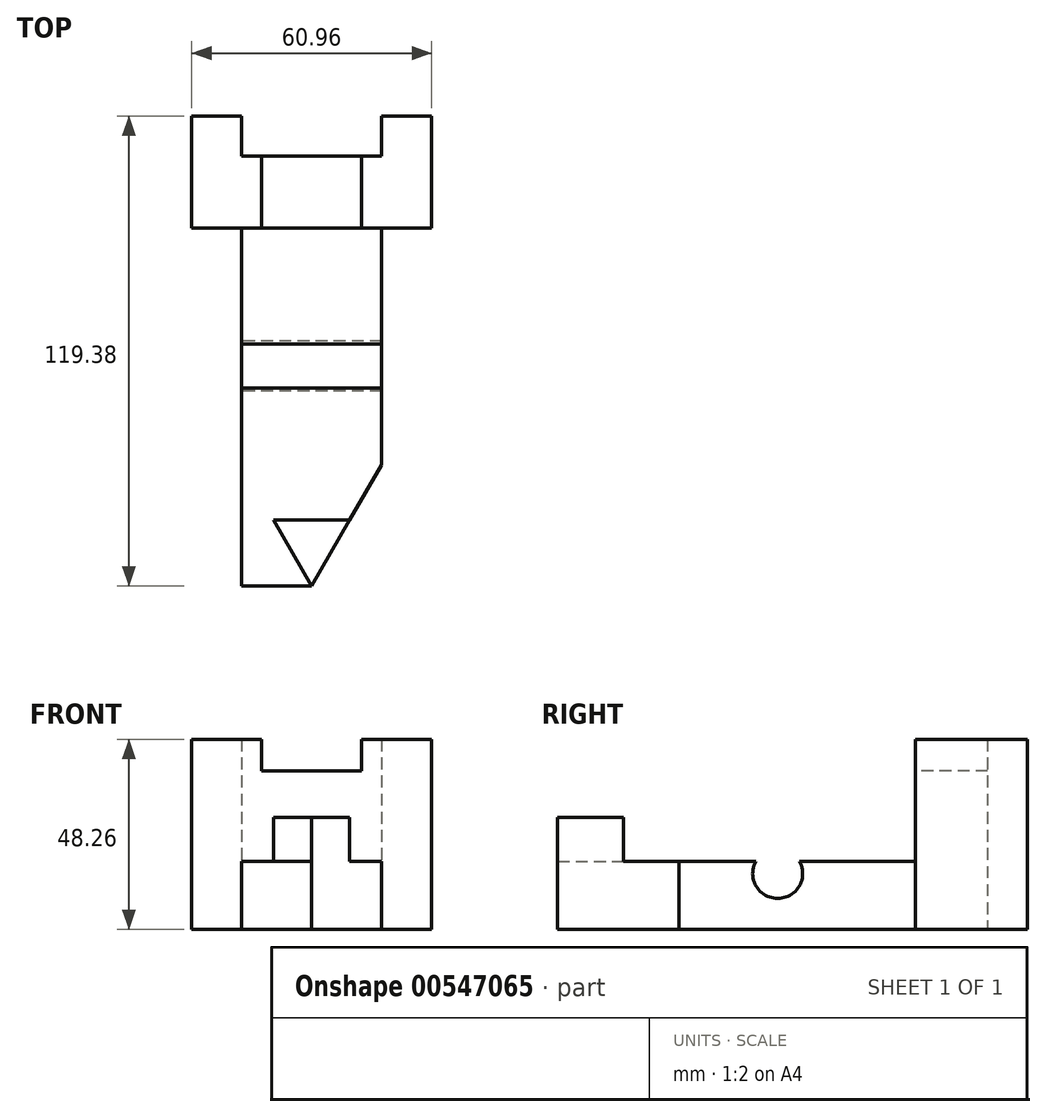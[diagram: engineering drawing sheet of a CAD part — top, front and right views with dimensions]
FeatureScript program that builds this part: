
annotation { "Feature Type Name" : "Feature", "Feature Type Description" : "" }
export const myFeature = defineFeature(function(context is Context, id is Id, definition is map)
    precondition{}
    {
        {
            var Q0;
            Q0=qCreatedBy(makeId("Front.planeOp"),FACE);
            var sketch = newSketch(context, id + "F0", { "sketchPlane" : qUnion([Q0])});
            skLineSegment(sketch, "E0.bottom", {"start": v(-43.38, 10.74) * mm, "end": v(17.58, 10.74) * mm});
            skLineSegment(sketch, "E0.top", {"start": v(-43.38, -37.52) * mm, "end": v(17.58, -37.52) * mm});
            skLineSegment(sketch, "E0.left", {"start": v(-43.38, 10.74) * mm, "end": v(-43.38, -37.52) * mm});
            skLineSegment(sketch, "E0.right", {"start": v(17.58, 10.74) * mm, "end": v(17.58, -37.52) * mm});
            skSolve(sketch);
        }
        {
            var Q0;
            Q0=makeQuery(id+"F0.imprint","IMPRINT",FACE,{"disambiguationData":[TD([[makeQuery(id+"F0.imprint","IMPRINT",EDGE,{"derivedFrom":sQuery(id+"F0.wireOp",EDGE,"E0.bottom")}),-1.0]])]});
            extrude(context, id + "F1", {"entities" : qUnion([Q0]), "depth" : 28.45 * mm, "offsetDistance" : 25.4 * mm});
        }
        {
            var Q0;
            Q0=makeQuery(id+"F1.opExtrude","CAP_FACE",FACE,{"disambiguationData":[OSD([sQuery(id+"F0.wireOp",EDGE,"E0.bottom"),sQuery(id+"F0.wireOp",EDGE,"E0.top"),sQuery(id+"F0.wireOp",EDGE,"E0.left"),sQuery(id+"F0.wireOp",EDGE,"E0.right")])],"isStart":false});
            var sketch = newSketch(context, id + "F2", { "sketchPlane" : qUnion([Q0])});
            skLineSegment(sketch, "E1.bottom", {"start": v(-25.6, 10.74) * mm, "end": v(-0.2, 10.74) * mm});
            skLineSegment(sketch, "E1.top", {"start": v(-25.6, 2.76) * mm, "end": v(-0.2, 2.76) * mm});
            skLineSegment(sketch, "E1.left", {"start": v(-25.6, 10.74) * mm, "end": v(-25.6, 2.76) * mm});
            skLineSegment(sketch, "E1.right", {"start": v(-0.2, 10.74) * mm, "end": v(-0.2, 2.76) * mm});
            skSolve(sketch);
        }
        {
            var Q0;
            Q0=makeQuery(id+"F2.imprint","IMPRINT",FACE,{"disambiguationData":[TD([[makeQuery(id+"F2.imprint","IMPRINT",EDGE,{"derivedFrom":sQuery(id+"F2.wireOp",EDGE,"E1.bottom")}),-1.0]])]});
            extrude(context, id + "F3", {"entities" : qUnion([Q0]), "operationType" : NewBodyOperationType.REMOVE, "oppositeDirection" : true, "depth" : 30.23 * mm, "offsetDistance" : 25.4 * mm});
        }
        {
            var Q0;
            Q0=makeQuery(id+"F1.opExtrude","CAP_FACE",FACE,{"disambiguationData":[OSD([sQuery(id+"F0.wireOp",EDGE,"E0.bottom"),sQuery(id+"F0.wireOp",EDGE,"E0.top"),sQuery(id+"F0.wireOp",EDGE,"E0.left"),sQuery(id+"F0.wireOp",EDGE,"E0.right")])],"isStart":true});
            var sketch = newSketch(context, id + "F4", { "sketchPlane" : qUnion([Q0])});
            skLineSegment(sketch, "E2.bottom", {"start": v(-4.88, 10.74) * mm, "end": v(30.68, 10.74) * mm});
            skLineSegment(sketch, "E2.top", {"start": v(-4.88, -37.52) * mm, "end": v(30.68, -37.52) * mm});
            skLineSegment(sketch, "E2.left", {"start": v(-4.88, 10.74) * mm, "end": v(-4.88, -37.52) * mm});
            skLineSegment(sketch, "E2.right", {"start": v(30.68, 10.74) * mm, "end": v(30.68, -37.52) * mm});
            skSolve(sketch);
        }
        {
            var Q0;
            Q0 = qSketchRegion(id + "F4", true);
            extrude(context, id + "F5", {"entities" : qUnion([Q0]), "operationType" : NewBodyOperationType.REMOVE, "oppositeDirection" : true, "depth" : 10.16 * mm, "offsetDistance" : 25.4 * mm});
        }
        {
            var Q0;
            Q0=makeQuery(id+"F1.opExtrude","CAP_FACE",FACE,{"disambiguationData":[OSD([sQuery(id+"F0.wireOp",EDGE,"E0.bottom"),sQuery(id+"F0.wireOp",EDGE,"E0.top"),sQuery(id+"F0.wireOp",EDGE,"E0.left"),sQuery(id+"F0.wireOp",EDGE,"E0.right")])],"isStart":false});
            var sketch = newSketch(context, id + "F6", { "sketchPlane" : qUnion([Q0])});
            skLineSegment(sketch, "E3.bottom", {"start": v(-30.68, -37.52) * mm, "end": v(4.88, -37.52) * mm});
            skLineSegment(sketch, "E3.top", {"start": v(-30.68, -9.07) * mm, "end": v(4.88, -9.07) * mm});
            skLineSegment(sketch, "E3.left", {"start": v(-30.68, -37.52) * mm, "end": v(-30.68, -9.07) * mm});
            skLineSegment(sketch, "E3.right", {"start": v(4.88, -37.52) * mm, "end": v(4.88, -9.07) * mm});
            skSolve(sketch);
        }
        {
            var Q0;
            Q0=makeQuery(id+"F6.imprint","IMPRINT",FACE,{"disambiguationData":[TD([[makeQuery(id+"F6.imprint","IMPRINT",EDGE,{"derivedFrom":sQuery(id+"F6.wireOp",EDGE,"E3.bottom")}),1.0]])]});
            extrude(context, id + "F7", {"entities" : qUnion([Q0]), "depth" : 90.93 * mm, "offsetDistance" : 25.4 * mm});
        }
        {
            var Q0;
            Q0=makeQuery(id+"F7.opExtrude","SWEPT_FACE",FACE,{"disambiguationData":[OSD([sQuery(id+"F6.wireOp",EDGE,"E3.left")])]});
            var sketch = newSketch(context, id + "F8", { "sketchPlane" : qUnion([Q0])});
            skCircle(sketch, "E4", {"center": v(63.5, -23.3) * mm, "radius": 6.35 * mm});
            skSolve(sketch);
        }
        {
            var Q0;
            Q0 = qSketchRegion(id + "F8", true);
            extrude(context, id + "F9", {"entities" : qUnion([Q0]), "operationType" : NewBodyOperationType.REMOVE, "oppositeDirection" : true, "depth" : 42.16 * mm, "offsetDistance" : 25.4 * mm});
        }
        {
            var Q0;
            Q0=makeQuery(id+"F7.opExtrude","SWEPT_FACE",FACE,{"disambiguationData":[OSD([sQuery(id+"F6.wireOp",EDGE,"E3.top")])]});
            var sketch = newSketch(context, id + "F10", { "sketchPlane" : qUnion([Q0])});
            skLineSegment(sketch, "E5", {"start": v(-12.9, -119.38) * mm, "end": v(-30.68, -88.58) * mm});
            skLineSegment(sketch, "E6", {"start": v(-30.68, -88.58) * mm, "end": v(-12.9, -119.38) * mm});
            skLineSegment(sketch, "E7", {"start": v(4.88, -88.58) * mm, "end": v(-12.9, -119.38) * mm});
            skPoint(sketch, "E8", {"position": v(-30.68, -73.91) * mm});
            skSolve(sketch);
        }
        {
            var Q0;
            Q0 = qSketchRegion(id + "F10", true);
            var Q1;
            {var subQ0=sQuery(id+"F10.wireOp",EDGE,"E6");Q1=makeQuery(id+"F10.imprint","IMPRINT",FACE,{"disambiguationData":[TD([[makeQuery(id+"F10.imprint","IMPRINT",EDGE,{"derivedFrom":subQ0}),-1.0]])]});}
            var Q2;
            {var subQ0=sQuery(id+"F10.wireOp",EDGE,"E7");Q2=makeQuery(id+"F10.imprint","IMPRINT",FACE,{"disambiguationData":[TD([[makeQuery(id+"F10.imprint","IMPRINT",EDGE,{"derivedFrom":subQ0}),1.0]])]});}
            extrude(context, id + "F11", {"entities" : qUnion([Q0, Q1, Q2]), "operationType" : NewBodyOperationType.REMOVE, "oppositeDirection" : true, "depth" : 32.77 * mm, "offsetDistance" : 25.4 * mm});
        }
        {
            var Q0;
            Q0=makeQuery(id+"F7.opExtrude","SWEPT_FACE",FACE,{"disambiguationData":[OSD([sQuery(id+"F6.wireOp",EDGE,"E3.top")])]});
            var sketch = newSketch(context, id + "F12", { "sketchPlane" : qUnion([Q0])});
            skLineSegment(sketch, "E9", {"start": v(-12.9, -119.38) * mm, "end": v(-22.55, -102.66) * mm});
            skLineSegment(sketch, "E10", {"start": v(-12.9, -119.38) * mm, "end": v(-3.25, -102.66) * mm});
            skLineSegment(sketch, "E11", {"start": v(-22.55, -102.66) * mm, "end": v(-3.25, -102.66) * mm});
            skSolve(sketch);
        }
        {
            var Q0;
            Q0=makeQuery(id+"F12.imprint","IMPRINT",FACE,{"disambiguationData":[TD([[makeQuery(id+"F12.imprint","IMPRINT",EDGE,{"derivedFrom":sQuery(id+"F12.wireOp",EDGE,"E9")}),1.0]])]});
            extrude(context, id + "F13", {"entities" : qUnion([Q0]), "operationType" : NewBodyOperationType.REMOVE, "oppositeDirection" : true, "depth" : 11.18 * mm, "offsetDistance" : 25.4 * mm});
        }
    });
